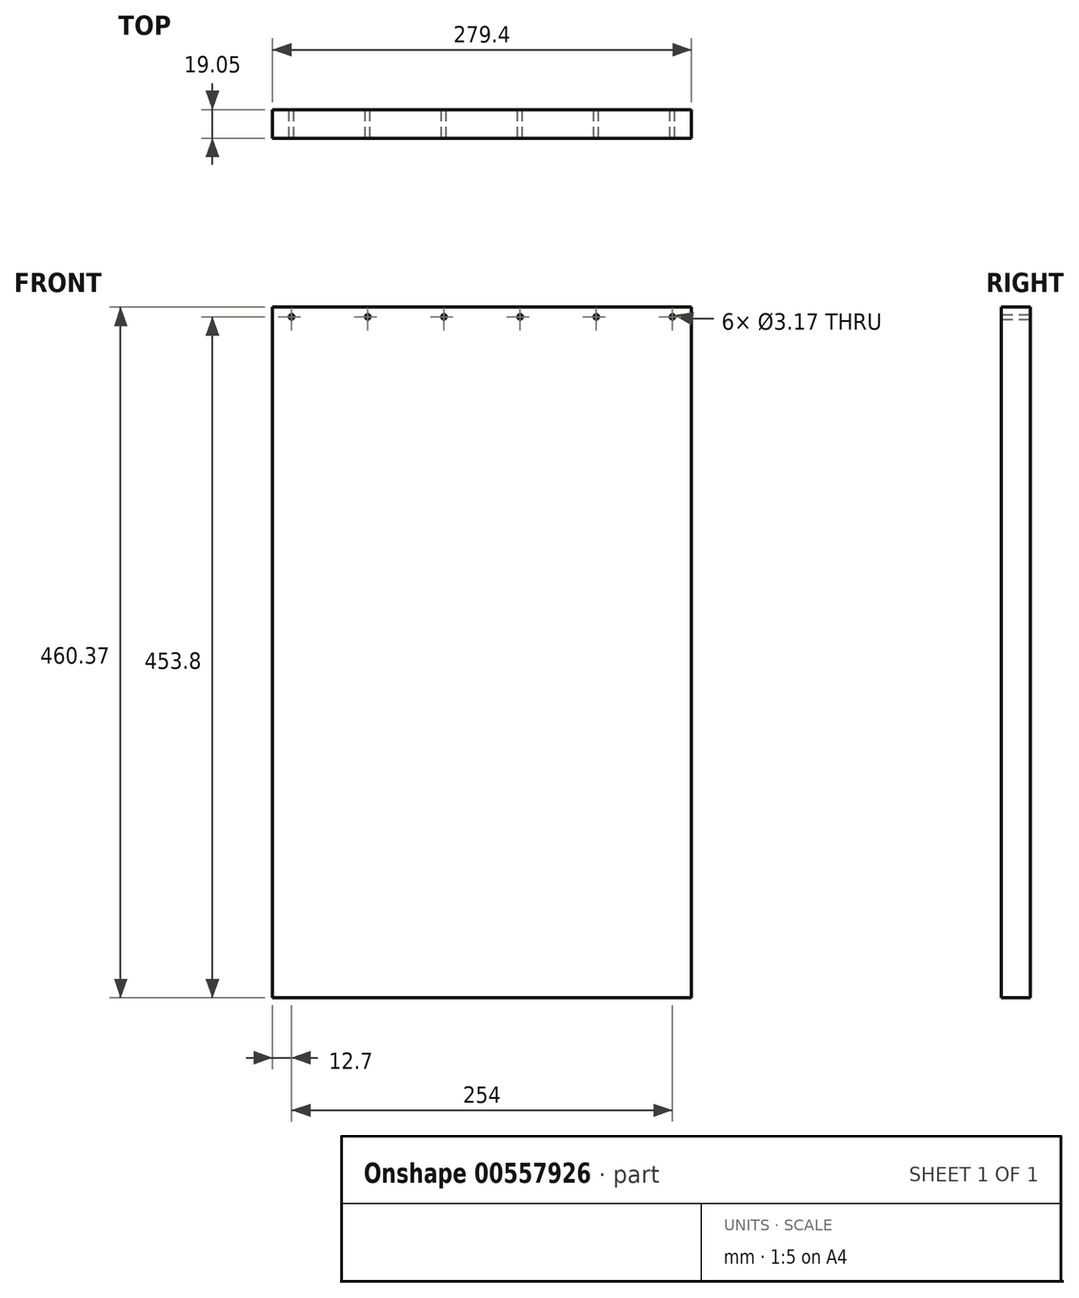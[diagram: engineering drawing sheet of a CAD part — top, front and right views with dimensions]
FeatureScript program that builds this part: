
annotation { "Feature Type Name" : "Feature", "Feature Type Description" : "" }
export const myFeature = defineFeature(function(context is Context, id is Id, definition is map)
    precondition{}
    {
        {
            var Q0;
            Q0=qCreatedBy(makeId("Front.planeOp"),FACE);
            var sketch = newSketch(context, id + "F0", { "sketchPlane" : qUnion([Q0])});
            skLineSegment(sketch, "E0.bottom", {"start": v(340.36, 511.17) * mm, "end": v(60.96, 511.17) * mm});
            skLineSegment(sketch, "E0.top", {"start": v(340.36, 50.8) * mm, "end": v(60.96, 50.8) * mm});
            skLineSegment(sketch, "E0.left", {"start": v(340.36, 511.17) * mm, "end": v(340.36, 50.8) * mm});
            skLineSegment(sketch, "E0.right", {"start": v(60.96, 511.17) * mm, "end": v(60.96, 50.8) * mm});
            skPoint(sketch, "E0.middle", {"position": v(200.66, 280.99) * mm});
            skCircle(sketch, "E1", {"center": v(73.66, 504.6) * mm, "radius": 1.59 * mm});
            skCircle(sketch, "E2", {"center": v(124.46, 504.6) * mm, "radius": 1.59 * mm});
            skCircle(sketch, "E3", {"center": v(175.26, 504.6) * mm, "radius": 1.59 * mm});
            skCircle(sketch, "E4.MirrorC", {"center": v(276.86, 504.6) * mm, "radius": 1.59 * mm});
            skCircle(sketch, "E5.MirrorC", {"center": v(226.06, 504.6) * mm, "radius": 1.59 * mm});
            skCircle(sketch, "E6.MirrorC", {"center": v(327.66, 504.6) * mm, "radius": 1.59 * mm});
            skSolve(sketch);
        }
        {
            var Q0;
            Q0=makeQuery(id+"F0.imprint","IMPRINT",FACE,{"disambiguationData":[TD([[makeQuery(id+"F0.imprint","IMPRINT",EDGE,{"derivedFrom":sQuery(id+"F0.wireOp",EDGE,"E0.bottom")}),1.0]])]});
            extrude(context, id + "F1", {"entities" : qUnion([Q0]), "depth" : 19.05 * mm, "offsetDistance" : 25.4 * mm});
        }
    });
